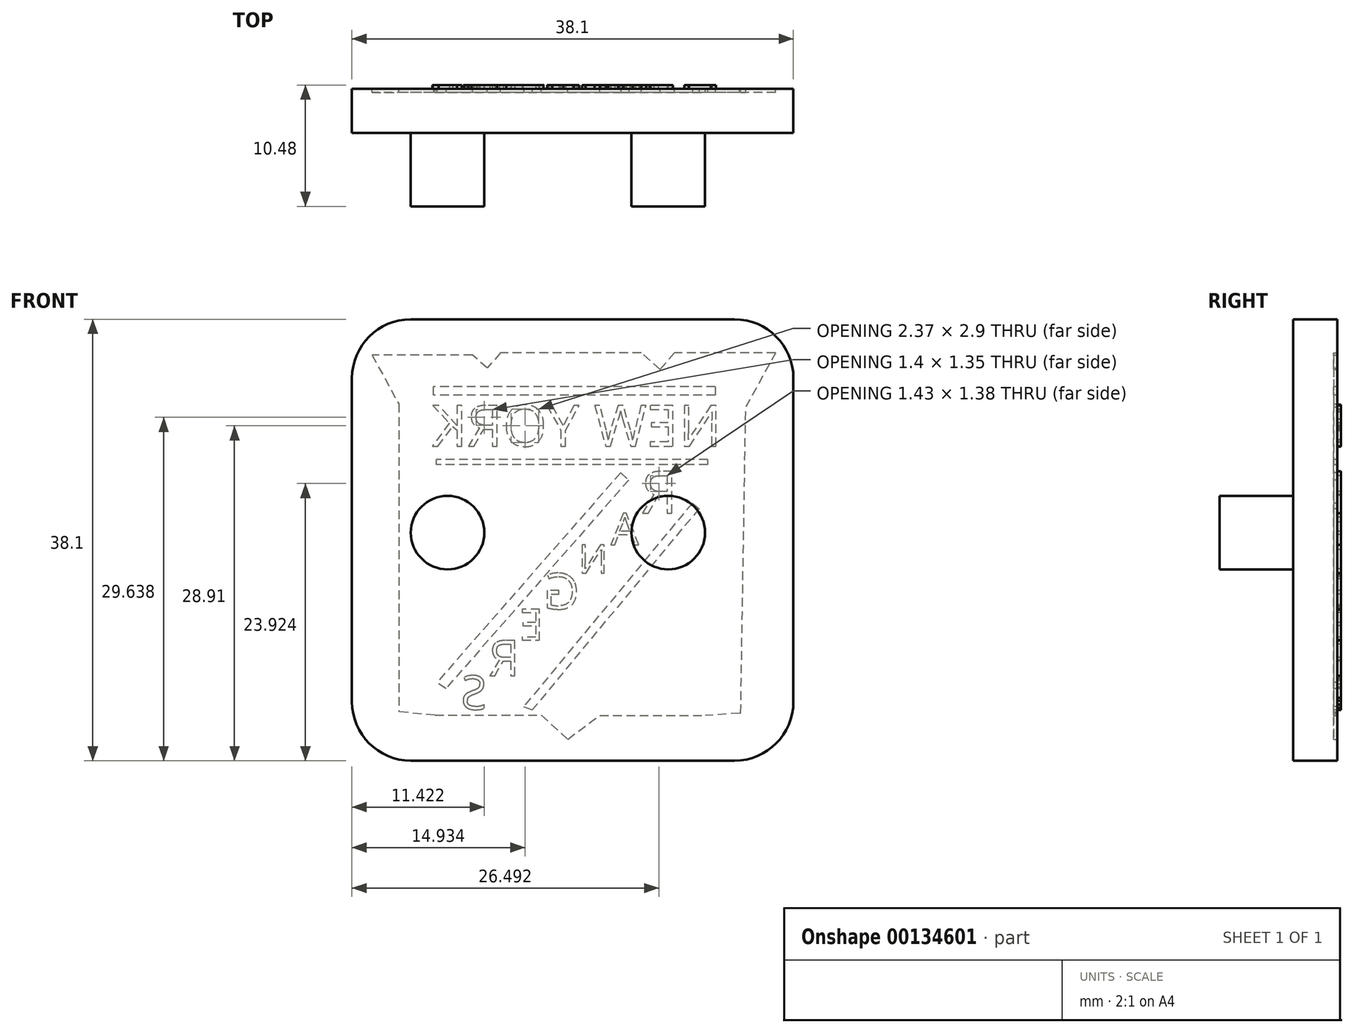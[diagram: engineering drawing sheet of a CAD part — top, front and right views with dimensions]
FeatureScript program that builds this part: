
annotation { "Feature Type Name" : "Feature", "Feature Type Description" : "" }
export const myFeature = defineFeature(function(context is Context, id is Id, definition is map)
    precondition{}
    {
        {
            var Q0;
            Q0=qCreatedBy(makeId("Front.planeOp"),FACE);
            cPlane(context, id + "F0", {"entities" : qUnion([Q0]), "cplaneType" : CPlaneType.OFFSET, "offset" : 25.4 * mm, "width" : 152.4 * mm, "height" : 152.4 * mm});
        }
        {
            var Q0;
            Q0=qCreatedBy(id+"F0.planeOp",FACE);
            var sketch = newSketch(context, id + "F1", { "sketchPlane" : qUnion([Q0])});
            skLineSegment(sketch, "E0.bottom", {"start": v(-40.48, 37.6) * mm, "end": v(-2.38, 37.6) * mm});
            skLineSegment(sketch, "E0.top", {"start": v(-40.48, -0.5) * mm, "end": v(-2.38, -0.5) * mm});
            skLineSegment(sketch, "E0.left", {"start": v(-40.48, 37.6) * mm, "end": v(-40.48, -0.5) * mm});
            skLineSegment(sketch, "E0.right", {"start": v(-2.38, 37.6) * mm, "end": v(-2.38, -0.5) * mm});
            skSolve(sketch);
        }
        {
            var Q0;
            Q0=makeQuery(id+"F1.imprint","IMPRINT",FACE,{"disambiguationData":[TD([[makeQuery(id+"F1.imprint","IMPRINT",EDGE,{"derivedFrom":sQuery(id+"F1.wireOp",EDGE,"E0.bottom")}),-1.0]])]});
            extrude(context, id + "F2", {"entities" : qUnion([Q0]), "depth" : 3.8 * mm});
        }
        {
            var Q0;
            Q0=makeQuery(id+"F2.opExtrude","CAP_FACE",FACE,{"disambiguationData":[OSD([sQuery(id+"F1.wireOp",EDGE,"E0.bottom"),sQuery(id+"F1.wireOp",EDGE,"E0.top"),sQuery(id+"F1.wireOp",EDGE,"E0.left"),sQuery(id+"F1.wireOp",EDGE,"E0.right")])],"isStart":false});
            var sketch = newSketch(context, id + "F3", { "sketchPlane" : qUnion([Q0])});
            skCircle(sketch, "E1", {"center": v(-32.22, 19.19) * mm, "radius": 3.18 * mm});
            skCircle(sketch, "E2", {"center": v(-13.17, 19.19) * mm, "radius": 3.18 * mm});
            skSolve(sketch);
        }
        {
            var Q0;
            Q0 = qSketchRegion(id + "F3", true);
            extrude(context, id + "F4", {"entities" : qUnion([Q0]), "operationType" : NewBodyOperationType.ADD, "depth" : 6.35 * mm});
        }
        {
            var Q0;
            Q0=makeQuery(id+"F2.opExtrude","SWEPT_EDGE",EDGE,{"disambiguationData":[OSD([sQuery(id+"F1.wireOp",EDGE,"E0.bottom"),sQuery(id+"F1.wireOp",EDGE,"E0.left")])]});
            var Q1;
            Q1=makeQuery(id+"F2.opExtrude","SWEPT_EDGE",EDGE,{"disambiguationData":[OSD([sQuery(id+"F1.wireOp",EDGE,"E0.bottom"),sQuery(id+"F1.wireOp",EDGE,"E0.right")])]});
            var Q2;
            Q2=makeQuery(id+"F2.opExtrude","SWEPT_EDGE",EDGE,{"disambiguationData":[OSD([sQuery(id+"F1.wireOp",EDGE,"E0.top"),sQuery(id+"F1.wireOp",EDGE,"E0.left")])]});
            var Q3;
            Q3=makeQuery(id+"F2.opExtrude","SWEPT_EDGE",EDGE,{"disambiguationData":[OSD([sQuery(id+"F1.wireOp",EDGE,"E0.top"),sQuery(id+"F1.wireOp",EDGE,"E0.right")])]});
            fillet(context, id + "F5", {"entities" : qUnion([Q0, Q1, Q2, Q3]), "radius" : 5.08 * mm, "tangentPropagation" : true, "allowEdgeOverflow" : false});
        }
        {
            var Q0;
            Q0=makeQuery(id+"F2.opExtrude","CAP_FACE",FACE,{"disambiguationData":[OSD([sQuery(id+"F1.wireOp",EDGE,"E0.bottom"),sQuery(id+"F1.wireOp",EDGE,"E0.top"),sQuery(id+"F1.wireOp",EDGE,"E0.left"),sQuery(id+"F1.wireOp",EDGE,"E0.right")])],"isStart":true});
            var sketch = newSketch(context, id + "F6", { "sketchPlane" : qUnion([Q0])});
            skPoint(sketch, "E3.secondSnap0", {"position": v(38.99, 1) * mm});
            skSolve(sketch);
        }
        {
            var Q0;
            {var subQ3=sQuery(id+"F1.wireOp",EDGE,"E0.bottom");Q0=makeQuery(id+"F6.imprint","IMPRINT",FACE,{"disambiguationData":[TD([[makeQuery(id+"F6.imprint","IMPRINT",EDGE,{"derivedFrom":makeQuery(id+"F2.opExtrude","CAP_EDGE",EDGE,{"disambiguationData":[OSD([subQ3])],"isStart":true})}),1.0]])]});}
            var sketch = newSketch(context, id + "F7", { "sketchPlane" : qUnion([Q0])});
            skLineSegment(sketch, "E4", {"start": v(3.91, 34.72) * mm, "end": v(6.49, 30.03) * mm});
            skLineSegment(sketch, "E5", {"start": v(3.91, 34.72) * mm, "end": v(12.63, 34.72) * mm});
            skLineSegment(sketch, "E6", {"start": v(12.63, 34.72) * mm, "end": v(13.88, 33.3) * mm});
            skLineSegment(sketch, "E7", {"start": v(13.88, 33.3) * mm, "end": v(15.5, 34.7) * mm});
            skLineSegment(sketch, "E8", {"start": v(15.5, 34.7) * mm, "end": v(27.65, 34.7) * mm});
            skLineSegment(sketch, "E9", {"start": v(27.65, 34.7) * mm, "end": v(28.8, 33.4) * mm});
            skLineSegment(sketch, "E10", {"start": v(28.8, 33.4) * mm, "end": v(30.09, 34.53) * mm});
            skLineSegment(sketch, "E11", {"start": v(30.4, 34.53) * mm, "end": v(38.73, 34.53) * mm});
            skLineSegment(sketch, "E12", {"start": v(38.73, 34.53) * mm, "end": v(36.44, 30.3) * mm});
            skLineSegment(sketch, "E13", {"start": v(36.44, 30.3) * mm, "end": v(36.44, 6.67) * mm});
            skLineSegment(sketch, "E14", {"start": v(33.31, 3.42) * mm, "end": v(24.12, 3.42) * mm});
            skLineSegment(sketch, "E15", {"start": v(24.12, 3.42) * mm, "end": v(21.85, 1.35) * mm});
            skLineSegment(sketch, "E16", {"start": v(21.85, 1.35) * mm, "end": v(19.09, 3.4) * mm});
            skLineSegment(sketch, "E17", {"start": v(19.09, 3.4) * mm, "end": v(9.97, 3.4) * mm});
            skLineSegment(sketch, "E18", {"start": v(6.88, 5.98) * mm, "end": v(6.49, 30.03) * mm});
            skLineSegment(sketch, "E19", {"start": v(36.44, 6.67) * mm, "end": v(36.44, 3.72) * mm});
            skLineSegment(sketch, "E20", {"start": v(33.31, 3.42) * mm, "end": v(36.44, 3.72) * mm});
            skLineSegment(sketch, "E21", {"start": v(6.88, 5.98) * mm, "end": v(6.92, 3.6) * mm});
            skLineSegment(sketch, "E22", {"start": v(7, 3.6) * mm, "end": v(9.97, 3.4) * mm});
            skLineSegment(sketch, "E23", {"start": v(6.92, 3.6) * mm, "end": v(7, 3.6) * mm});
            skLineSegment(sketch, "E24", {"start": v(30.4, 34.53) * mm, "end": v(30.09, 34.53) * mm});
            skSolve(sketch);
        }
        {
            var Q0;
            {var subQ3=sQuery(id+"F1.wireOp",EDGE,"E0.bottom");Q0=makeQuery(id+"F6.imprint","IMPRINT",FACE,{"disambiguationData":[TD([[makeQuery(id+"F6.imprint","IMPRINT",EDGE,{"derivedFrom":makeQuery(id+"F2.opExtrude","CAP_EDGE",EDGE,{"disambiguationData":[OSD([subQ3])],"isStart":true})}),1.0]])]});}
            var sketch = newSketch(context, id + "F8", { "sketchPlane" : qUnion([Q0])});
            skText(sketch, "E25", { "text": "NEW YORK", "fontName": "OpenSans-Regular.ttf"});
            skText(sketch, "E26", { "text": "R", "fontName": "OpenSans-Regular.ttf"});
            skText(sketch, "E27", { "text": "A", "fontName": "OpenSans-Regular.ttf"});
            skText(sketch, "E28", { "text": "N", "fontName": "OpenSans-Regular.ttf"});
            skText(sketch, "E29", { "text": "G", "fontName": "OpenSans-Regular.ttf"});
            skText(sketch, "E30", { "text": "E", "fontName": "OpenSans-Regular.ttf"});
            skText(sketch, "E31", { "text": "R", "fontName": "OpenSans-Regular.ttf"});
            skText(sketch, "E32", { "text": "S", "fontName": "OpenSans-Regular.ttf"});
            const initialGuessF8  = {"E25": [0.00856, 0.02665, 1, 0, 0.00355], "E26": [0.01236, 0.02088, 1, 0, 0.00363], "E27": [0.01572, 0.01815, 1, 0, 0.00273], "E28": [0.01836, 0.01568, 1, 0, 0.00246], "E29": [0.02083, 0.0126, 1, 0, 0.00309], "E30": [0.02392, 0.0099, 1, 0, 0.0027], "E31": [0.02601, 0.00684, 1, 0, 0.00306], "E32": [0.02884, 0.00393, 1, 0, 0.00292]};
            skSetInitialGuess(sketch, initialGuessF8);
            skSolve(sketch);
        }
        {
            var Q0;
            Q0 = qSketchRegion(id + "F7", true);
            extrude(context, id + "F9", {"entities" : qUnion([Q0]), "operationType" : NewBodyOperationType.REMOVE, "oppositeDirection" : true, "depth" : 0.32 * mm});
        }
        {
            var Q0;
            Q0 = qSketchRegion(id + "F8", true);
            extrude(context, id + "F10", {"entities" : qUnion([Q0]), "depth" : 0.32 * mm});
        }
        {
            var Q0;
            Q0=makeQuery(id+"F9.boolean.opBoolean","COPY",FACE,{"derivedFrom":makeQuery(id+"F9.opExtrude","CAP_FACE",FACE,{"disambiguationData":[OSD([sQuery(id+"F7.wireOp",EDGE,"E4"),sQuery(id+"F7.wireOp",EDGE,"E5"),sQuery(id+"F7.wireOp",EDGE,"E6"),sQuery(id+"F7.wireOp",EDGE,"E7"),sQuery(id+"F7.wireOp",EDGE,"E8"),sQuery(id+"F7.wireOp",EDGE,"E9"),sQuery(id+"F7.wireOp",EDGE,"E10"),sQuery(id+"F7.wireOp",EDGE,"E11"),sQuery(id+"F7.wireOp",EDGE,"E12"),sQuery(id+"F7.wireOp",EDGE,"E13"),sQuery(id+"F7.wireOp",EDGE,"E14"),sQuery(id+"F7.wireOp",EDGE,"E15"),sQuery(id+"F7.wireOp",EDGE,"E16"),sQuery(id+"F7.wireOp",EDGE,"E17"),sQuery(id+"F7.wireOp",EDGE,"E18"),sQuery(id+"F7.wireOp",EDGE,"E19"),sQuery(id+"F7.wireOp",EDGE,"E20"),sQuery(id+"F7.wireOp",EDGE,"E21"),sQuery(id+"F7.wireOp",EDGE,"E22"),sQuery(id+"F7.wireOp",EDGE,"E23"),sQuery(id+"F7.wireOp",EDGE,"E24")])],"isStart":false})});
            var sketch = newSketch(context, id + "F11", { "sketchPlane" : qUnion([Q0])});
            skLineSegment(sketch, "E33", {"start": v(9.11, 31.8) * mm, "end": v(33.45, 31.8) * mm});
            skLineSegment(sketch, "E34", {"start": v(9.78, 25.5) * mm, "end": v(33.17, 25.5) * mm});
            skLineSegment(sketch, "E35", {"start": v(17.29, 24.35) * mm, "end": v(33.14, 6.25) * mm});
            skLineSegment(sketch, "E36", {"start": v(11.1, 21.73) * mm, "end": v(25.67, 4.15) * mm});
            skLineSegment(sketch, "E37", {"start": v(9.78, 25.5) * mm, "end": v(9.78, 25.05) * mm});
            skLineSegment(sketch, "E38", {"start": v(9.78, 25.05) * mm, "end": v(33.17, 25.05) * mm});
            skLineSegment(sketch, "E39", {"start": v(33.17, 25.05) * mm, "end": v(33.17, 25.5) * mm});
            skLineSegment(sketch, "E40", {"start": v(9.11, 31.8) * mm, "end": v(9.11, 31.05) * mm});
            skLineSegment(sketch, "E41", {"start": v(9.11, 31.05) * mm, "end": v(33.44, 31.05) * mm});
            skLineSegment(sketch, "E42", {"start": v(33.44, 31.05) * mm, "end": v(33.45, 31.8) * mm});
            skLineSegment(sketch, "E43", {"start": v(11.1, 21.73) * mm, "end": v(10.53, 21.26) * mm});
            skLineSegment(sketch, "E44", {"start": v(10.53, 21.26) * mm, "end": v(24.92, 3.88) * mm});
            skLineSegment(sketch, "E45", {"start": v(24.92, 3.88) * mm, "end": v(25.67, 4.15) * mm});
            skLineSegment(sketch, "E46", {"start": v(17.29, 24.35) * mm, "end": v(16.58, 23.74) * mm});
            skLineSegment(sketch, "E47", {"start": v(16.58, 23.74) * mm, "end": v(32.36, 5.72) * mm});
            skLineSegment(sketch, "E48", {"start": v(32.36, 5.72) * mm, "end": v(33.14, 6.25) * mm});
            skSolve(sketch);
        }
        {
            var Q0;
            Q0 = qSketchRegion(id + "F11", true);
            extrude(context, id + "F12", {"entities" : qUnion([Q0]), "operationType" : NewBodyOperationType.ADD, "depth" : 0.32 * mm});
        }
    });
